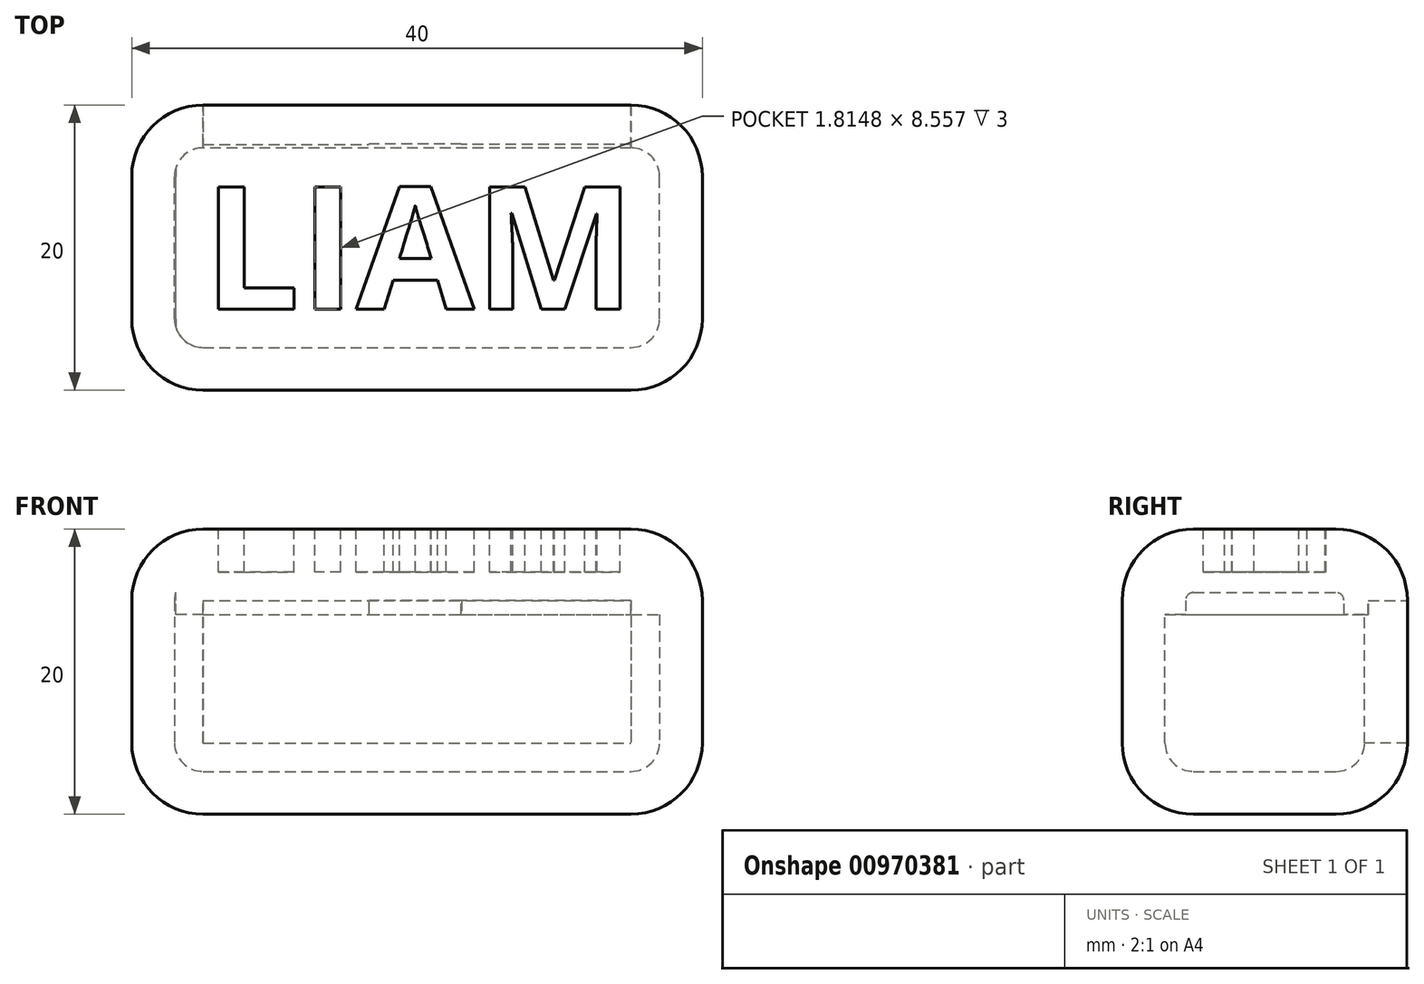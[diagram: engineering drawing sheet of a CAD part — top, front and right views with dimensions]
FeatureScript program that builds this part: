
annotation { "Feature Type Name" : "Feature", "Feature Type Description" : "" }
export const myFeature = defineFeature(function(context is Context, id is Id, definition is map)
    precondition{}
    {
        {
            var Q0;
            Q0=qCreatedBy(makeId("Top.planeOp"),FACE);
            var sketch = newSketch(context, id + "F0", { "sketchPlane" : qUnion([Q0])});
            skLineSegment(sketch, "E0.bottom", {"start": v(-20, 10) * mm, "end": v(20, 10) * mm});
            skLineSegment(sketch, "E0.top", {"start": v(-20, -10) * mm, "end": v(20, -10) * mm});
            skLineSegment(sketch, "E0.left", {"start": v(-20, 10) * mm, "end": v(-20, -10) * mm});
            skLineSegment(sketch, "E0.right", {"start": v(20, 10) * mm, "end": v(20, -10) * mm});
            skPoint(sketch, "E1", {"position": v(-20, 0) * mm});
            skLineSegment(sketch, "E2", {"start": v(-20, 0) * mm, "end": v(20, 0) * mm, "construction": true});
            skPoint(sketch, "E3", {"position": v(0, 0) * mm});
            skSolve(sketch);
        }
        {
            var Q0;
            Q0=makeQuery(id+"F0.imprint","IMPRINT",FACE,{"disambiguationData":[TD([[makeQuery(id+"F0.imprint","IMPRINT",EDGE,{"derivedFrom":sQuery(id+"F0.wireOp",EDGE,"E0.bottom")}),-1.0]])]});
            extrude(context, id + "F1", {"entities" : qUnion([Q0]), "depth" : 20 * mm, "offsetDistance" : 25.4 * mm});
        }
        {
            var Q0;
            Q0=makeQuery(id+"F1.opExtrude","CAP_FACE",FACE,{"disambiguationData":[OSD([sQuery(id+"F0.wireOp",EDGE,"E0.bottom"),sQuery(id+"F0.wireOp",EDGE,"E0.top"),sQuery(id+"F0.wireOp",EDGE,"E0.left"),sQuery(id+"F0.wireOp",EDGE,"E0.right")])],"isStart":false});
            var sketch = newSketch(context, id + "F2", { "sketchPlane" : qUnion([Q0])});
            skText(sketch, "E4", { "text": "LIAM", "fontName": "OpenSans-Bold.ttf"});
            const initialGuessF2  = {"E4": [-0.015, -0.00431, 1, 0, 0.00863]};
            skSetInitialGuess(sketch, initialGuessF2);
            skSolve(sketch);
        }
        {
            var Q0;
            Q0=makeQuery(id+"F2.imprint","IMPRINT",FACE,{"disambiguationData":[TD([[makeQuery(id+"F2.imprint","IMPRINT",EDGE,{"derivedFrom":sQuery(id+"F2.wireOp",EDGE,"E4.sketch_text.stroke-0")}),-1.0]])]});
            var Q1;
            Q1=makeQuery(id+"F2.imprint","IMPRINT",FACE,{"disambiguationData":[TD([[makeQuery(id+"F2.imprint","IMPRINT",EDGE,{"derivedFrom":sQuery(id+"F2.wireOp",EDGE,"E4.sketch_text.stroke-6")}),-1.0]])]});
            var Q2;
            Q2=makeQuery(id+"F2.imprint","IMPRINT",FACE,{"disambiguationData":[TD([[makeQuery(id+"F2.imprint","IMPRINT",EDGE,{"derivedFrom":sQuery(id+"F2.wireOp",EDGE,"E4.sketch_text.stroke-10")}),-1.0]])]});
            var Q3;
            Q3=makeQuery(id+"F2.imprint","IMPRINT",FACE,{"disambiguationData":[TD([[makeQuery(id+"F2.imprint","IMPRINT",EDGE,{"derivedFrom":sQuery(id+"F2.wireOp",EDGE,"E4.sketch_text.stroke-22")}),-1.0]])]});
            extrude(context, id + "F3", {"entities" : qUnion([Q0, Q1, Q2, Q3]), "operationType" : NewBodyOperationType.REMOVE, "oppositeDirection" : true, "depth" : 3 * mm, "offsetDistance" : 25 * mm});
        }
        {
            var Q0;
            Q0=makeQuery(id+"F1.opExtrude","SWEPT_FACE",FACE,{"disambiguationData":[OSD([sQuery(id+"F0.wireOp",EDGE,"E0.top")])]});
            var Q1;
            Q1=makeQuery(id+"F1.opExtrude","SWEPT_FACE",FACE,{"disambiguationData":[OSD([sQuery(id+"F0.wireOp",EDGE,"E0.left")])]});
            var Q2;
            Q2=makeQuery(id+"F1.opExtrude","SWEPT_FACE",FACE,{"disambiguationData":[OSD([sQuery(id+"F0.wireOp",EDGE,"E0.bottom")])]});
            var Q3;
            Q3=makeQuery(id+"F1.opExtrude","SWEPT_FACE",FACE,{"disambiguationData":[OSD([sQuery(id+"F0.wireOp",EDGE,"E0.right")])]});
            fillet(context, id + "F4", {"entities" : qUnion([Q0, Q1, Q2, Q3]), "radius" : 5 * mm, "tangentPropagation" : true, "defaultsChanged" : false, "vertexSettings" : [], "allowEdgeOverflow" : false});
        }
        {
            var Q0;
            Q0=makeQuery(id+"F1.opExtrude","SWEPT_FACE",FACE,{"disambiguationData":[OSD([sQuery(id+"F0.wireOp",EDGE,"E0.bottom")])]});
            shell(context, id + "F5", {"entities" : qUnion([Q0]), "thickness" : 3 * mm});
        }
    });
